# Revit family: Aluco Fire SL 2P (HI) (en)
name_source: partatom
category: Generic Models
units: mm (PartAtom-declared; Revit-internal decimal feet)

## family parameters
Always vertical = No
Can host rebar = No
Cut with Voids When Loaded = Yes
OmniClass Number = 23.60.70.14.11
OmniClass Title = Smoke Dampers
Part Type = Normal
Room Calculation Point = No
Round Connector Dimension = Use Diameter
Shared = No
Work Plane-Based = Yes

## types (6) — shared parameters
Confirmed performance in extremely low temperatures = T -15
Deflector material = Aluco - galvanized steel
Description = Double-leaf vent dedicated to barrel vault skylights
Fire protection class = BRoof (t1)
High temperature resistance class = B 300
IfcExportAs = "IfcWindowType"
Manufacturer = ALUCO SYSTEM SP. Z O.O
Maximum snow load = SL 1500
Opening angle = 90.00°
Panel material = Aluco - polycarbonate
Product URL = https://aluco.com.pl
Profile material = Aluco - aluminum
Reliability of operation = RE 10000
Safety classification against drop from height = SB 1200
Type Image = ALUCO FIRE SL 1P (HI).png
URL = https://aluco.com.pl
Wind exposure classification = WL 1500
zero-valued in all types: Default Elevation

## per-type parameters (varying)
| type | Bridge-free system | Drive type | Economic system | Model | Power supply | Type Comments |
| economical system with pneumatic drive | No | pneumatic drive | Yes | FIRE SL 2P | 0 V | Smoke damper in a economical system |
| bridge-free system with pneumatic drive | Yes | pneumatic drive | No | FIRE SL 2P (HI) | 0 V | Smoke damper in a bridge-free system with increased thermal insulation |
| bridge-free system with electric drive | Yes | electric drive | No | FIRE SL 2P (HI) | 230 V | Smoke damper in a bridge-free system with increased thermal insulation |
| economical system with electric drive | Yes | electric drive | No | FIRE SL 2P (HI) | 230 V | Smoke damper in a economical system |
| economical system with pneumatic-electric drive | Yes | pneumatic-electric drive | No | FIRE SL 2P (HI) | 230 V | Smoke damper in a economical system |
| bridge-free system with pneumatic-electric drive | Yes | pneumatic-electric drive | No | FIRE SL 2P (HI) | 230 V | Smoke damper in a bridge-free system with increased thermal insulation |
